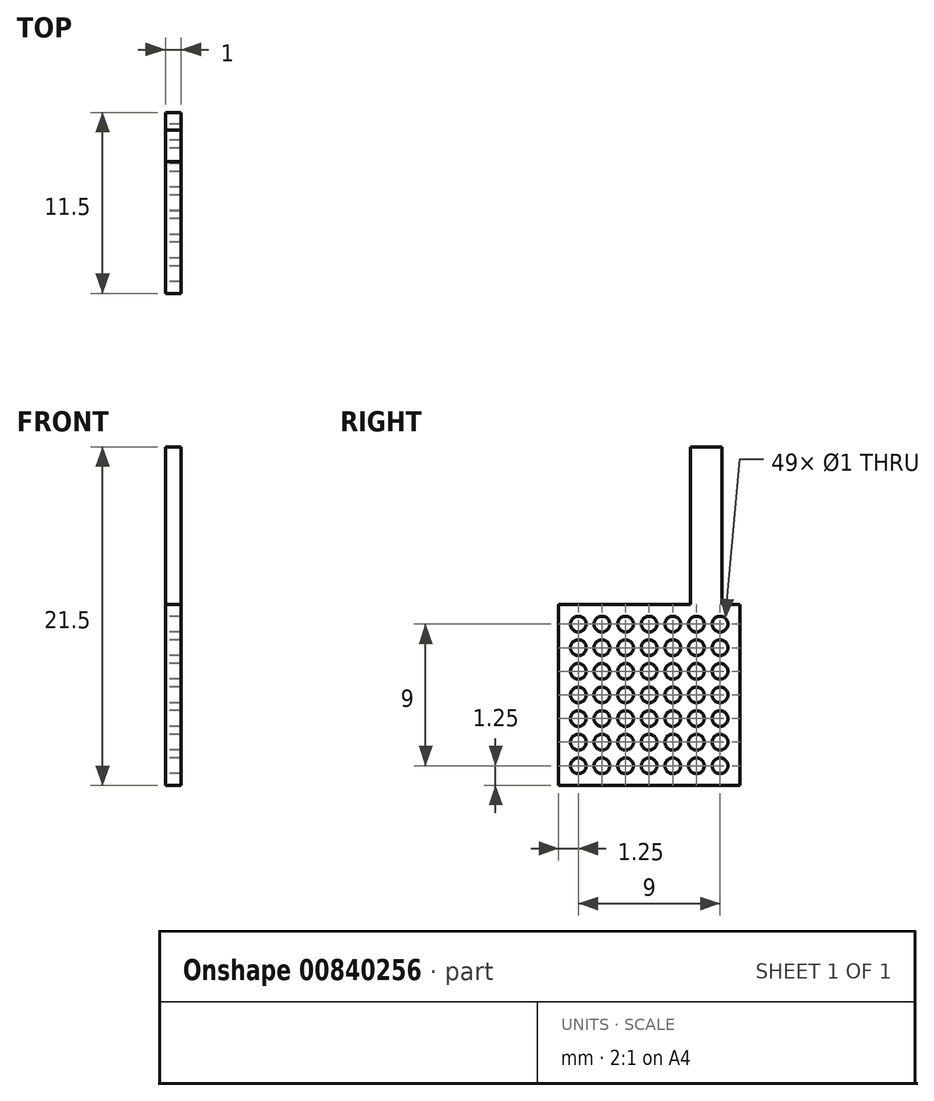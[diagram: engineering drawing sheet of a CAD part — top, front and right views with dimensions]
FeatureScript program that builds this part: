
annotation { "Feature Type Name" : "Feature", "Feature Type Description" : "" }
export const myFeature = defineFeature(function(context is Context, id is Id, definition is map)
    precondition{}
    {
        {
            var Q0;
            Q0=qCreatedBy(makeId("Right.planeOp"),FACE);
            var sketch = newSketch(context, id + "F0", { "sketchPlane" : qUnion([Q0])});
            skLineSegment(sketch, "E0.bottom", {"start": v(0, 0) * mm, "end": v(8.38, 0) * mm});
            skLineSegment(sketch, "E0.top", {"start": v(0, -11.5) * mm, "end": v(11.5, -11.5) * mm});
            skLineSegment(sketch, "E0.left", {"start": v(0, 0) * mm, "end": v(0, -11.5) * mm});
            skCircle(sketch, "E1", {"center": v(5.75, -5.75) * mm, "radius": 0.5 * mm});
            skLineSegment(sketch, "E2", {"start": v(11.5, 0) * mm, "end": v(11.5, -11.5) * mm});
            skCircle(sketch, "E3", {"center": v(5.75, -4.25) * mm, "radius": 0.5 * mm});
            skCircle(sketch, "E4", {"center": v(5.75, -2.75) * mm, "radius": 0.5 * mm});
            skCircle(sketch, "E5", {"center": v(4.25, -5.75) * mm, "radius": 0.5 * mm});
            skCircle(sketch, "E6", {"center": v(5.75, -1.25) * mm, "radius": 0.5 * mm});
            skCircle(sketch, "E7", {"center": v(4.25, -4.25) * mm, "radius": 0.5 * mm});
            skCircle(sketch, "E8", {"center": v(4.25, -2.75) * mm, "radius": 0.5 * mm});
            skCircle(sketch, "E9", {"center": v(4.25, -1.25) * mm, "radius": 0.5 * mm});
            skCircle(sketch, "E10", {"center": v(2.75, -5.75) * mm, "radius": 0.5 * mm});
            skCircle(sketch, "E11", {"center": v(2.75, -4.25) * mm, "radius": 0.5 * mm});
            skCircle(sketch, "E12", {"center": v(2.75, -2.75) * mm, "radius": 0.5 * mm});
            skCircle(sketch, "E13", {"center": v(2.75, -1.25) * mm, "radius": 0.5 * mm});
            skCircle(sketch, "E14", {"center": v(1.25, -5.75) * mm, "radius": 0.5 * mm});
            skCircle(sketch, "E15", {"center": v(1.25, -4.25) * mm, "radius": 0.5 * mm});
            skCircle(sketch, "E16", {"center": v(1.25, -2.75) * mm, "radius": 0.5 * mm});
            skCircle(sketch, "E17", {"center": v(1.25, -1.25) * mm, "radius": 0.5 * mm});
            skCircle(sketch, "E18.MirrorC", {"center": v(7.25, -1.25) * mm, "radius": 0.5 * mm});
            skCircle(sketch, "E19.MirrorC", {"center": v(7.25, -2.75) * mm, "radius": 0.5 * mm});
            skCircle(sketch, "E20.MirrorC", {"center": v(7.25, -4.25) * mm, "radius": 0.5 * mm});
            skCircle(sketch, "E21.MirrorC", {"center": v(7.25, -5.75) * mm, "radius": 0.5 * mm});
            skCircle(sketch, "E22.MirrorC", {"center": v(8.75, -5.75) * mm, "radius": 0.5 * mm});
            skCircle(sketch, "E23.MirrorC", {"center": v(8.75, -4.25) * mm, "radius": 0.5 * mm});
            skCircle(sketch, "E24.MirrorC", {"center": v(8.75, -2.75) * mm, "radius": 0.5 * mm});
            skCircle(sketch, "E25.MirrorC", {"center": v(8.75, -1.25) * mm, "radius": 0.5 * mm});
            skCircle(sketch, "E26.MirrorC", {"center": v(10.25, -1.25) * mm, "radius": 0.5 * mm});
            skCircle(sketch, "E27.MirrorC", {"center": v(10.25, -2.75) * mm, "radius": 0.5 * mm});
            skCircle(sketch, "E28.MirrorC", {"center": v(10.25, -4.25) * mm, "radius": 0.5 * mm});
            skCircle(sketch, "E29.MirrorC", {"center": v(10.25, -5.75) * mm, "radius": 0.5 * mm});
            skCircle(sketch, "E30.MirrorC", {"center": v(1.25, -7.25) * mm, "radius": 0.5 * mm});
            skCircle(sketch, "E31.MirrorC", {"center": v(2.75, -7.25) * mm, "radius": 0.5 * mm});
            skCircle(sketch, "E32.MirrorC", {"center": v(4.25, -7.25) * mm, "radius": 0.5 * mm});
            skCircle(sketch, "E33.MirrorC", {"center": v(4.25, -8.75) * mm, "radius": 0.5 * mm});
            skCircle(sketch, "E34.MirrorC", {"center": v(2.75, -8.75) * mm, "radius": 0.5 * mm});
            skCircle(sketch, "E35.MirrorC", {"center": v(1.25, -8.75) * mm, "radius": 0.5 * mm});
            skCircle(sketch, "E36.MirrorC", {"center": v(1.25, -10.25) * mm, "radius": 0.5 * mm});
            skCircle(sketch, "E37.MirrorC", {"center": v(2.75, -10.25) * mm, "radius": 0.5 * mm});
            skCircle(sketch, "E38.MirrorC", {"center": v(4.25, -10.25) * mm, "radius": 0.5 * mm});
            skCircle(sketch, "E39.MirrorC", {"center": v(5.75, -10.25) * mm, "radius": 0.5 * mm});
            skCircle(sketch, "E40.MirrorC", {"center": v(5.75, -8.75) * mm, "radius": 0.5 * mm});
            skCircle(sketch, "E41.MirrorC", {"center": v(5.75, -7.25) * mm, "radius": 0.5 * mm});
            skCircle(sketch, "E42.MirrorC", {"center": v(7.25, -7.25) * mm, "radius": 0.5 * mm});
            skCircle(sketch, "E43.MirrorC", {"center": v(7.25, -8.75) * mm, "radius": 0.5 * mm});
            skCircle(sketch, "E44.MirrorC", {"center": v(7.25, -10.25) * mm, "radius": 0.5 * mm});
            skCircle(sketch, "E45.MirrorC", {"center": v(8.75, -10.25) * mm, "radius": 0.5 * mm});
            skCircle(sketch, "E46.MirrorC", {"center": v(8.75, -8.75) * mm, "radius": 0.5 * mm});
            skCircle(sketch, "E47.MirrorC", {"center": v(8.75, -7.25) * mm, "radius": 0.5 * mm});
            skCircle(sketch, "E48.MirrorC", {"center": v(10.25, -7.25) * mm, "radius": 0.5 * mm});
            skCircle(sketch, "E49.MirrorC", {"center": v(10.25, -8.75) * mm, "radius": 0.5 * mm});
            skCircle(sketch, "E50.MirrorC", {"center": v(10.25, -10.25) * mm, "radius": 0.5 * mm});
            skLineSegment(sketch, "E51", {"start": v(10.38, 0) * mm, "end": v(10.38, 10) * mm});
            skLineSegment(sketch, "E52", {"start": v(10.38, 10) * mm, "end": v(8.38, 10) * mm});
            skLineSegment(sketch, "E53", {"start": v(8.38, 10) * mm, "end": v(8.38, 0) * mm});
            skLineSegment(sketch, "E54.trimOffspring", {"start": v(10.38, 0) * mm, "end": v(11.5, 0) * mm});
            skSolve(sketch);
        }
        {
            var Q0;
            Q0=makeQuery(id+"F0.imprint","IMPRINT",FACE,{"disambiguationData":[TD([[makeQuery(id+"F0.imprint","IMPRINT",EDGE,{"derivedFrom":sQuery(id+"F0.wireOp",EDGE,"E0.bottom")}),-1.0]])]});
            var Q1;
            Q1=makeQuery(id+"F0.imprint","IMPRINT",FACE,{"disambiguationData":[TD([[makeQuery(id+"F0.imprint","IMPRINT",EDGE,{"derivedFrom":sQuery(id+"F0.wireOp",EDGE,"r65wuaeR-pUGk-UfhY-v5oq-7bkjaNJfQmKm.bottom")}),-1.0]])]});
            var Q2;
            Q2=makeQuery(id+"F0.imprint","IMPRINT",FACE,{"disambiguationData":[TD([[makeQuery(id+"F0.imprint","IMPRINT",EDGE,{"derivedFrom":sQuery(id+"F0.wireOp",EDGE,"n5EaUuf3-CoM6-EQkv-XzT1-ydr3onYee1LO.bottom")}),1.0]])]});
            var Q3;
            Q3=makeQuery(id+"F0.imprint","IMPRINT",FACE,{"disambiguationData":[TD([[makeQuery(id+"F0.imprint","IMPRINT",EDGE,{"derivedFrom":sQuery(id+"F0.wireOp",EDGE,"2NUbogVr-x7fL-9LVX-WR3f-6RiyyzUn8nbi.bottom")}),-1.0]])]});
            extrude(context, id + "F1", {"entities" : qUnion([Q0, Q1, Q2, Q3]), "depth" : 1 * mm, "offsetDistance" : 25 * mm});
        }
    });
